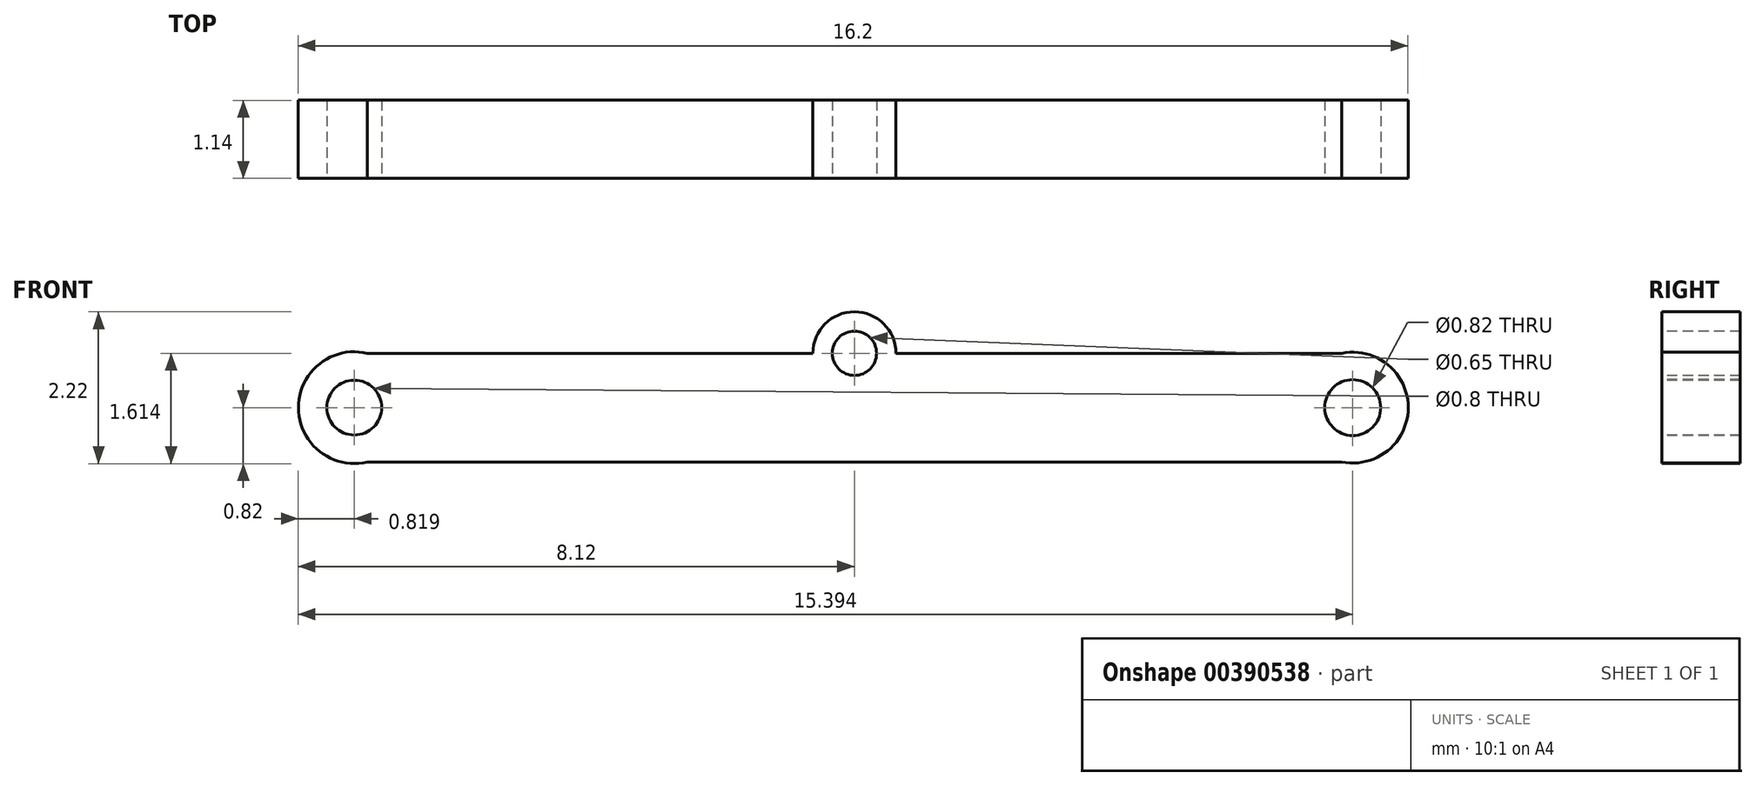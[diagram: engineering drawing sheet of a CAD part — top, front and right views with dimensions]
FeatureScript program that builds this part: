
annotation { "Feature Type Name" : "Feature", "Feature Type Description" : "" }
export const myFeature = defineFeature(function(context is Context, id is Id, definition is map)
    precondition{}
    {
        {
            var Q0;
            Q0=qCreatedBy(makeId("Front.planeOp"),FACE);
            var sketch = newSketch(context, id + "F0", { "sketchPlane" : qUnion([Q0])});
            skLineSegment(sketch, "E0.bottom", {"start": v(-7.11, -0.8) * mm, "end": v(7.11, -0.8) * mm});
            skLineSegment(sketch, "E0.top", {"start": v(-7.11, 0.8) * mm, "end": v(7.11, 0.8) * mm});
            skLineSegment(sketch, "E0.left", {"start": v(-7.11, -0.8) * mm, "end": v(-7.11, 0.8) * mm});
            skLineSegment(sketch, "E0.right", {"start": v(7.11, -0.8) * mm, "end": v(7.11, 0.8) * mm});
            skPoint(sketch, "E0.middle", {"position": v(0, 0) * mm});
            skArc(sketch, "E1", {"start": v(-0.6, 0.8) * mm, "mid": v(0, 1.4) * mm, "end": v(0.6, 0.8) * mm});
            skArc(sketch, "E2", {"start": v(-7.11, 0.8) * mm, "mid": v(-8.12, 0) * mm, "end": v(-7.11, -0.8) * mm});
            skArc(sketch, "E3", {"start": v(7.11, -0.8) * mm, "mid": v(8.08, 0) * mm, "end": v(7.11, 0.8) * mm});
            skSolve(sketch);
        }
        {
            var Q0;
            Q0 = qSketchRegion(id + "F0", true);
            extrude(context, id + "F1", {"entities" : qUnion([Q0]), "endBound" : BoundingType.SYMMETRIC, "depth" : 1.14 * mm});
        }
        {
            var Q0;
            Q0=makeQuery(id+"F1.opExtrude","CAP_FACE",FACE,{"disambiguationData":[OSD([sQuery(id+"F0.wireOp",EDGE,"E0.bottom"),sQuery(id+"F0.wireOp",EDGE,"E0.top"),sQuery(id+"F0.wireOp",EDGE,"E1"),sQuery(id+"F0.wireOp",EDGE,"E2"),sQuery(id+"F0.wireOp",EDGE,"E3")])],"isStart":false});
            var sketch = newSketch(context, id + "F2", { "sketchPlane" : qUnion([Q0])});
            skCircle(sketch, "E4", {"center": v(7.27, 0) * mm, "radius": 0.4 * mm});
            skCircle(sketch, "E5", {"center": v(-7.3, 0) * mm, "radius": 0.4 * mm});
            skCircle(sketch, "E6", {"center": v(0, 0.8) * mm, "radius": 0.32 * mm});
            skSolve(sketch);
        }
        {
            var Q0;
            Q0=makeQuery(id+"F2.imprint","IMPRINT",FACE,{"disambiguationData":[TD([[makeQuery(id+"F2.imprint","IMPRINT",EDGE,{"derivedFrom":sQuery(id+"F2.wireOp",EDGE,"E5")}),1.0]])]});
            var Q1;
            Q1=makeQuery(id+"F2.imprint","IMPRINT",FACE,{"disambiguationData":[TD([[makeQuery(id+"F2.imprint","IMPRINT",EDGE,{"derivedFrom":sQuery(id+"F2.wireOp",EDGE,"E6")}),1.0]])]});
            var Q2;
            Q2=makeQuery(id+"F2.imprint","IMPRINT",FACE,{"disambiguationData":[TD([[makeQuery(id+"F2.imprint","IMPRINT",EDGE,{"derivedFrom":sQuery(id+"F2.wireOp",EDGE,"E4")}),1.0]])]});
            extrude(context, id + "F3", {"entities" : qUnion([Q0, Q1, Q2]), "operationType" : NewBodyOperationType.REMOVE, "oppositeDirection" : true, "depth" : 25.4 * mm});
        }
    });
